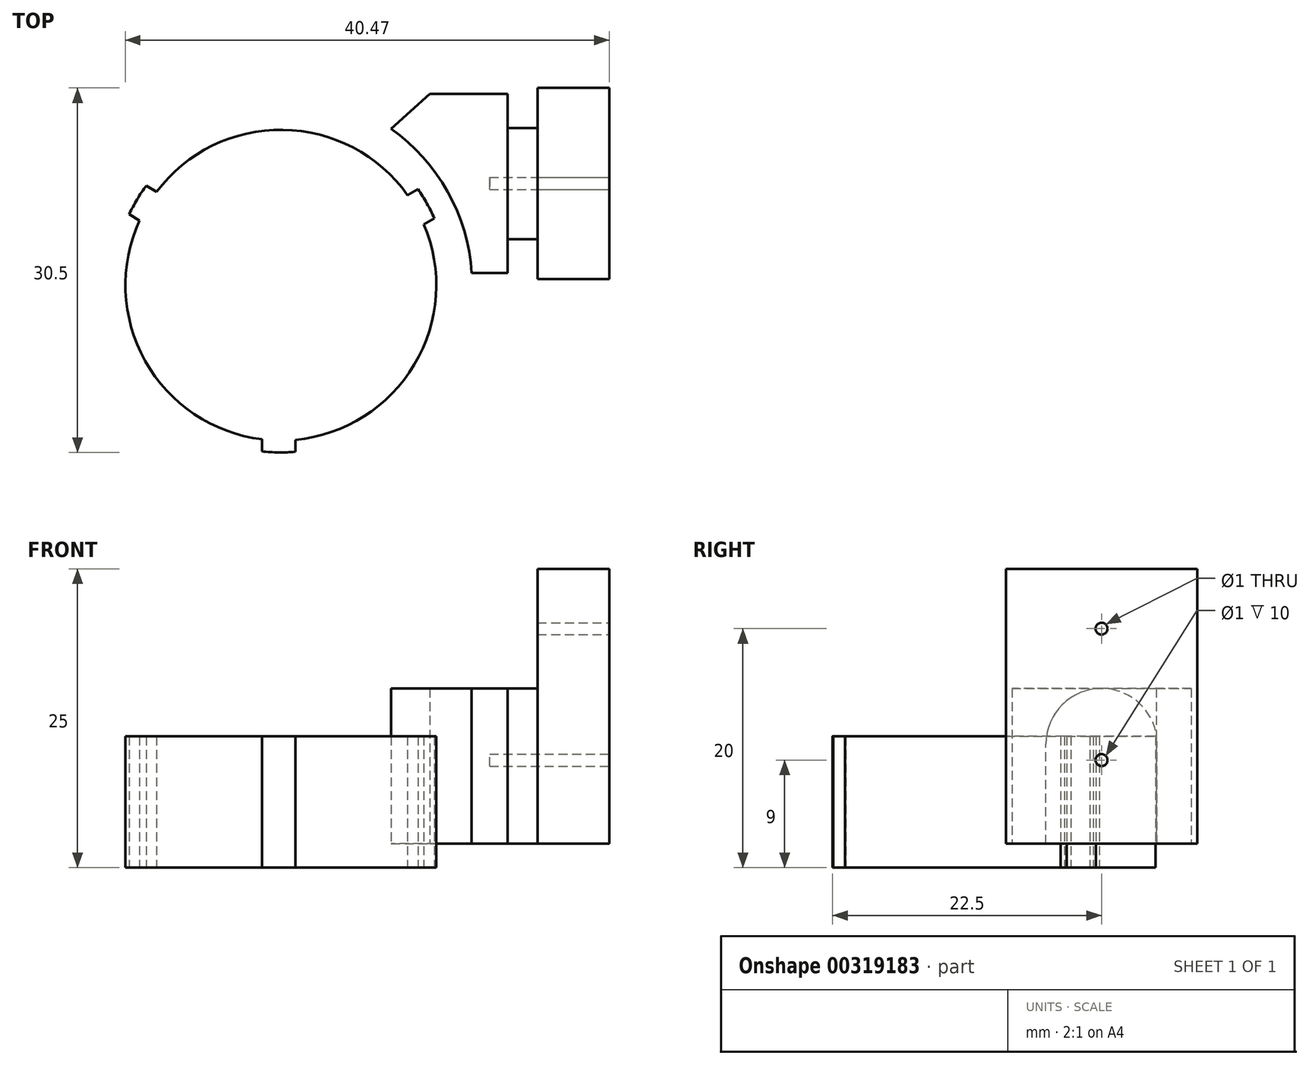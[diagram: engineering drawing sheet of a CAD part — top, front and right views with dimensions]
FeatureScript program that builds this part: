
annotation { "Feature Type Name" : "Feature", "Feature Type Description" : "" }
export const myFeature = defineFeature(function(context is Context, id is Id, definition is map)
    precondition{}
    {
        {
            var Q0;
            Q0=qCreatedBy(makeId("Top.planeOp"),FACE);
            var sketch = newSketch(context, id + "F0", { "sketchPlane" : qUnion([Q0])});
            skCircle(sketch, "E0", {"center": v(0, 0) * mm, "radius": 13 * mm, "construction": true});
            skCircle(sketch, "E1", {"center": v(0, 0) * mm, "radius": 16 * mm});
            skLineSegment(sketch, "E2", {"start": v(9.21, 13.08) * mm, "end": v(12.47, 16) * mm});
            skLineSegment(sketch, "E3", {"start": v(12.47, 16) * mm, "end": v(18.97, 16) * mm});
            skLineSegment(sketch, "E4", {"start": v(18.97, 16) * mm, "end": v(18.97, 1) * mm});
            skLineSegment(sketch, "E5", {"start": v(18.97, 1) * mm, "end": v(15.97, 1) * mm});
            skLineSegment(sketch, "E6", {"start": v(0, 0) * mm, "end": v(99.79, 0) * mm, "construction": true});
            skLineSegment(sketch, "E7", {"start": v(13.96, 7.81) * mm, "end": v(0, 0) * mm, "construction": true});
            skArc(sketch, "E8", {"start": v(11.47, 8.02) * mm, "mid": v(12.22, 6.83) * mm, "end": v(12.84, 5.58) * mm});
            skLineSegment(sketch, "E9", {"start": v(12.84, 5.58) * mm, "end": v(11.96, 5.09) * mm});
            skLineSegment(sketch, "E10", {"start": v(11.47, 8.02) * mm, "end": v(10.6, 7.53) * mm});
            skLineSegment(sketch, "E11.1.0", {"start": v(-12.68, 5.93) * mm, "end": v(-11.82, 5.41) * mm});
            skArc(sketch, "E11.1.1", {"start": v(-12.68, 5.93) * mm, "mid": v(-12.03, 7.16) * mm, "end": v(-11.25, 8.33) * mm});
            skLineSegment(sketch, "E11.1.2", {"start": v(-11.25, 8.33) * mm, "end": v(-10.39, 7.82) * mm});
            skLineSegment(sketch, "E11.2.0", {"start": v(1.21, -13.95) * mm, "end": v(1.22, -12.94) * mm});
            skArc(sketch, "E11.2.1", {"start": v(1.21, -13.95) * mm, "mid": v(-0.2, -14) * mm, "end": v(-1.59, -13.9) * mm});
            skLineSegment(sketch, "E11.2.2", {"start": v(-1.59, -13.9) * mm, "end": v(-1.58, -12.9) * mm});
            skArc(sketch, "E12", {"start": v(10.6, 7.53) * mm, "mid": v(0.18, 13) * mm, "end": v(-10.39, 7.82) * mm});
            skArc(sketch, "E13", {"start": v(-11.82, 5.41) * mm, "mid": v(-11.35, -6.35) * mm, "end": v(-1.58, -12.9) * mm});
            skArc(sketch, "E14", {"start": v(1.22, -12.94) * mm, "mid": v(11.17, -6.65) * mm, "end": v(11.96, 5.09) * mm});
            skSolve(sketch);
        }
        {
            var Q0;
            Q0=makeQuery(id+"F0.imprint","IMPRINT",FACE,{"disambiguationData":[TD([[makeQuery(id+"F0.imprint","IMPRINT",EDGE,{"derivedFrom":sQuery(id+"F0.wireOp",EDGE,"E0")}),-1.0]])]});
            var Q1;
            Q1=makeQuery(id+"F0.imprint","IMPRINT",FACE,{"disambiguationData":[TD([[makeQuery(id+"F0.imprint","IMPRINT",EDGE,{"derivedFrom":sQuery(id+"F0.wireOp",EDGE,"E8")}),1.0]])]});
            var Q2;
            {var subQ0=sQuery(id+"F0.wireOp",EDGE,"E2");Q2=makeQuery(id+"F0.imprint","IMPRINT",FACE,{"disambiguationData":[TD([[makeQuery(id+"F0.imprint","IMPRINT",EDGE,{"derivedFrom":subQ0}),-1.0]])]});}
            extrude(context, id + "F1", {"entities" : qUnion([Q0, Q1, Q2]), "depth" : 9 * mm});
        }
        {
            var Q0;
            {var subQ0=sQuery(id+"F0.wireOp",EDGE,"E2");Q0=makeQuery(id+"F0.imprint","IMPRINT",FACE,{"disambiguationData":[TD([[makeQuery(id+"F0.imprint","IMPRINT",EDGE,{"derivedFrom":subQ0}),-1.0]])]});}
            extrude(context, id + "F2", {"entities" : qUnion([Q0]), "operationType" : NewBodyOperationType.ADD, "depth" : 13 * mm});
        }
        {
            var Q0;
            Q0=makeQuery(id+"F2.opExtrude","SWEPT_FACE",FACE,{"disambiguationData":[OSD([sQuery(id+"F0.wireOp",EDGE,"E4")])]});
            var sketch = newSketch(context, id + "F3", { "sketchPlane" : qUnion([Q0])});
            skLineSegment(sketch, "E15", {"start": v(8.5, 13) * mm, "end": v(8.5, 0) * mm, "construction": true});
            skLineSegment(sketch, "E16", {"start": v(3.85, 0) * mm, "end": v(3.85, 8.35) * mm});
            skLineSegment(sketch, "E17", {"start": v(13.15, 0) * mm, "end": v(13.15, 8.35) * mm});
            skArc(sketch, "E18", {"start": v(3.85, 8.35) * mm, "mid": v(8.5, 13) * mm, "end": v(13.15, 8.35) * mm});
            skSolve(sketch);
        }
        {
            var Q0;
            {var subQ4=sQuery(id+"F3.wireOp",EDGE,"E16");Q0=makeQuery(id+"F3.imprint","IMPRINT",FACE,{"disambiguationData":[TD([[makeQuery(id+"F3.imprint","IMPRINT",EDGE,{"derivedFrom":subQ4}),-1.0]])]});}
            extrude(context, id + "F4", {"entities" : qUnion([Q0]), "operationType" : NewBodyOperationType.ADD, "depth" : 2.5 * mm});
        }
        {
            var Q0;
            Q0=makeQuery(id+"F4.opExtrude","CAP_FACE",FACE,{"disambiguationData":[OSD([sQuery(id+"F0.wireOp",EDGE,"E4"),sQuery(id+"F3.wireOp",EDGE,"E16"),sQuery(id+"F3.wireOp",EDGE,"E17"),sQuery(id+"F3.wireOp",EDGE,"E18")])],"isStart":false});
            var sketch = newSketch(context, id + "F5", { "sketchPlane" : qUnion([Q0])});
            skLineSegment(sketch, "E19", {"start": v(0.5, 0) * mm, "end": v(0.5, 23) * mm});
            skLineSegment(sketch, "E20", {"start": v(0.5, 23) * mm, "end": v(16.5, 23) * mm});
            skLineSegment(sketch, "E21", {"start": v(16.5, 23) * mm, "end": v(16.5, 0) * mm});
            skLineSegment(sketch, "E22", {"start": v(16.5, 0) * mm, "end": v(0.5, 0) * mm});
            skLineSegment(sketch, "E23", {"start": v(8.5, 13) * mm, "end": v(8.5, 0) * mm, "construction": true});
            skSolve(sketch);
        }
        {
            var Q0;
            {var subQ3=sQuery(id+"F5.wireOp",EDGE,"E19");Q0=makeQuery(id+"F5.imprint","IMPRINT",FACE,{"disambiguationData":[TD([[makeQuery(id+"F5.imprint","IMPRINT",EDGE,{"derivedFrom":subQ3}),-1.0]])]});}
            var Q1;
            {var subQ1=makeQuery(id+"F4.opExtrude","CAP_EDGE",EDGE,{"disambiguationData":[OSD([sQuery(id+"F3.wireOp",EDGE,"E16")])],"isStart":false});Q1=makeQuery(id+"F5.imprint","IMPRINT",FACE,{"disambiguationData":[TD([[makeQuery(id+"F5.imprint","IMPRINT",EDGE,{"derivedFrom":subQ1}),-1.0]])]});}
            extrude(context, id + "F6", {"entities" : qUnion([Q0, Q1]), "operationType" : NewBodyOperationType.ADD, "depth" : 6 * mm});
        }
        {
            var Q0;
            Q0=makeQuery(id+"F6.opExtrude","CAP_FACE",FACE,{"disambiguationData":[OSD([sQuery(id+"F5.wireOp",EDGE,"E19"),sQuery(id+"F5.wireOp",EDGE,"E20"),sQuery(id+"F5.wireOp",EDGE,"E21"),sQuery(id+"F5.wireOp",EDGE,"E22")])],"isStart":false});
            var sketch = newSketch(context, id + "F7", { "sketchPlane" : qUnion([Q0])});
            skLineSegment(sketch, "E24", {"start": v(8.5, 23) * mm, "end": v(8.5, 0) * mm, "construction": true});
            skCircle(sketch, "E25", {"center": v(8.5, 18) * mm, "radius": 0.5 * mm});
            skCircle(sketch, "E26", {"center": v(8.5, 7) * mm, "radius": 0.5 * mm});
            skSolve(sketch);
        }
        {
            var Q0;
            Q0=makeQuery(id+"F7.imprint","IMPRINT",FACE,{"disambiguationData":[TD([[makeQuery(id+"F7.imprint","IMPRINT",EDGE,{"derivedFrom":sQuery(id+"F7.wireOp",EDGE,"E26")}),1.0]])]});
            var Q1;
            Q1=makeQuery(id+"F7.imprint","IMPRINT",FACE,{"disambiguationData":[TD([[makeQuery(id+"F7.imprint","IMPRINT",EDGE,{"derivedFrom":sQuery(id+"F7.wireOp",EDGE,"E25")}),1.0]])]});
            extrude(context, id + "F8", {"entities" : qUnion([Q0, Q1]), "operationType" : NewBodyOperationType.REMOVE, "oppositeDirection" : true, "depth" : 10 * mm});
        }
        {
            var Q0;
            Q0=makeQuery(id+"F0.imprint","IMPRINT",FACE,{"disambiguationData":[TD([[makeQuery(id+"F0.imprint","IMPRINT",EDGE,{"derivedFrom":sQuery(id+"F0.wireOp",EDGE,"E8")}),1.0]])]});
            extrude(context, id + "F9", {"entities" : qUnion([Q0]), "operationType" : NewBodyOperationType.ADD, "depth" : -2 * mm});
        }
    });
